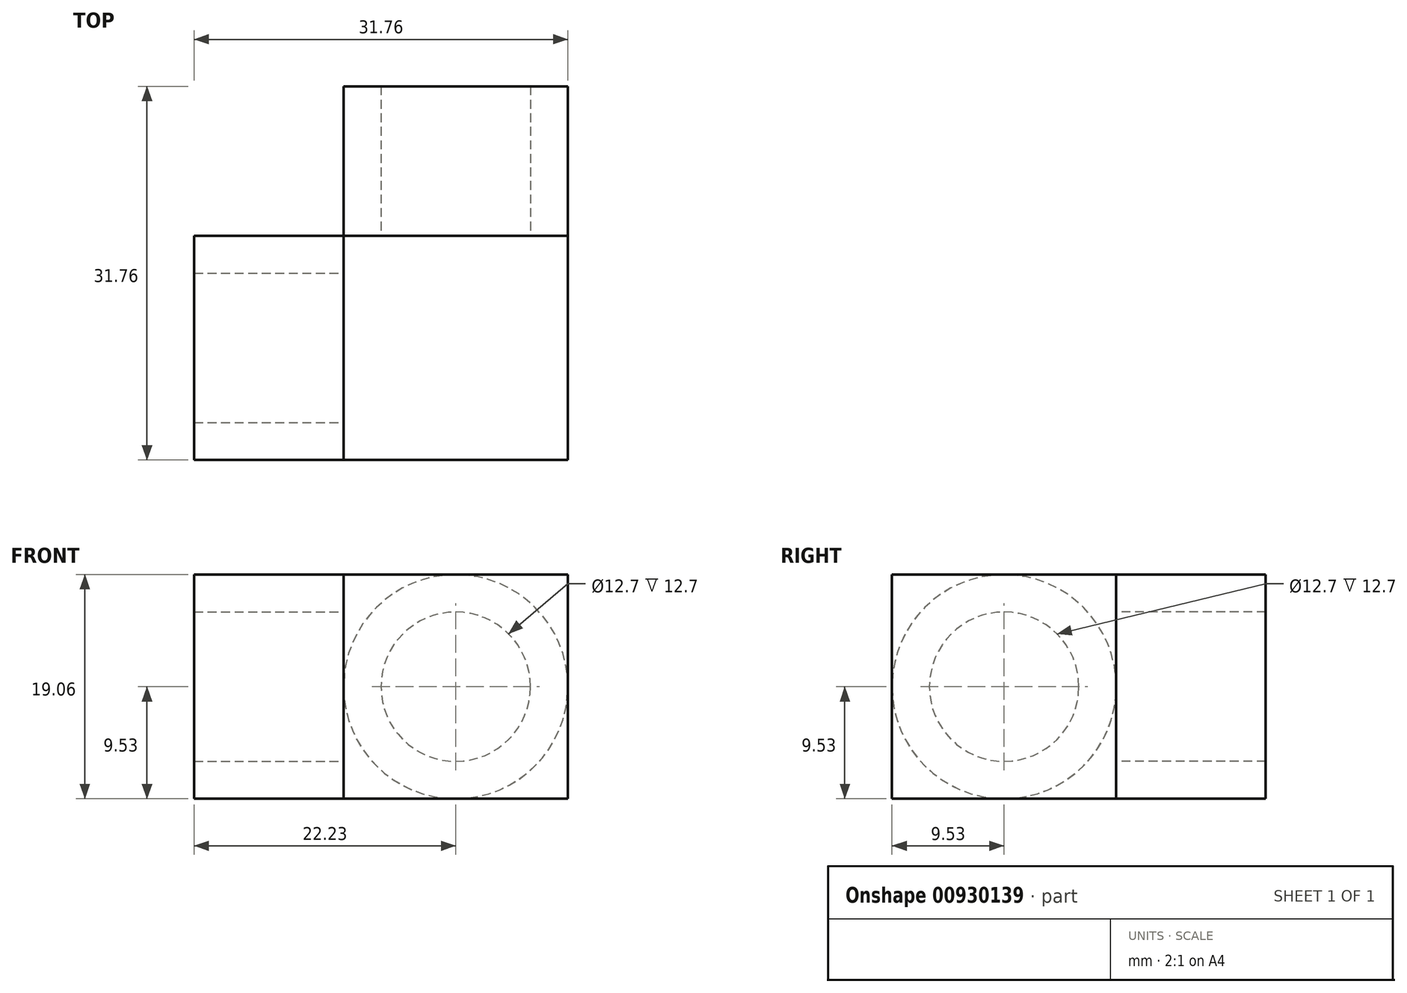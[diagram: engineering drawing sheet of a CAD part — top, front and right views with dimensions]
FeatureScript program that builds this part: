
annotation { "Feature Type Name" : "Feature", "Feature Type Description" : "" }
export const myFeature = defineFeature(function(context is Context, id is Id, definition is map)
    precondition{}
    {
        {
            var Q0;
            Q0=qCreatedBy(makeId("Top.planeOp"),FACE);
            var sketch = newSketch(context, id + "F0", { "sketchPlane" : qUnion([Q0])});
            skLineSegment(sketch, "E0.bottom", {"start": v(-9.53, -9.53) * mm, "end": v(9.53, -9.53) * mm});
            skLineSegment(sketch, "E0.top", {"start": v(-9.53, 9.53) * mm, "end": v(9.53, 9.53) * mm});
            skLineSegment(sketch, "E0.left", {"start": v(-9.53, -9.53) * mm, "end": v(-9.53, 9.53) * mm});
            skLineSegment(sketch, "E0.right", {"start": v(9.53, -9.52) * mm, "end": v(9.53, 9.53) * mm});
            skPoint(sketch, "E0.middle", {"position": v(0, 0) * mm});
            skSolve(sketch);
        }
        {
            var Q0;
            Q0 = qSketchRegion(id + "F0", true);
            extrude(context, id + "F1", {"entities" : qUnion([Q0]), "depth" : 19.05 * mm, "offsetDistance" : 25.4 * mm, "symmetric" : true});
        }
        {
            var Q0;
            Q0=makeQuery(id+"F1.opExtrude","SWEPT_FACE",FACE,{"disambiguationData":[OSD([sQuery(id+"F0.wireOp",EDGE,"E0.top")])]});
            var sketch = newSketch(context, id + "F2", { "sketchPlane" : qUnion([Q0])});
            skCircle(sketch, "E1", {"center": v(0, 0) * mm, "radius": 6.35 * mm});
            skCircle(sketch, "E2", {"center": v(0, 0) * mm, "radius": 9.53 * mm});
            skSolve(sketch);
        }
        {
            var Q0;
            Q0=makeQuery(id+"F2.imprint","IMPRINT",FACE,{"disambiguationData":[TD([[makeQuery(id+"F2.imprint","IMPRINT",EDGE,{"derivedFrom":sQuery(id+"F2.wireOp",EDGE,"E1")}),-1.0]])]});
            extrude(context, id + "F3", {"entities" : qUnion([Q0]), "operationType" : NewBodyOperationType.ADD, "depth" : 12.7 * mm, "offsetDistance" : 25.4 * mm});
        }
        {
            var Q0;
            Q0=makeQuery(id+"F1.opExtrude","SWEPT_FACE",FACE,{"disambiguationData":[OSD([sQuery(id+"F0.wireOp",EDGE,"E0.left")])]});
            var sketch = newSketch(context, id + "F4", { "sketchPlane" : qUnion([Q0])});
            skCircle(sketch, "E3", {"center": v(0, 0) * mm, "radius": 6.35 * mm});
            skCircle(sketch, "E4", {"center": v(0, 0) * mm, "radius": 9.53 * mm});
            skSolve(sketch);
        }
        {
            var Q0;
            Q0 = qSketchRegion(id + "F4", true);
            extrude(context, id + "F5", {"entities" : qUnion([Q0]), "operationType" : NewBodyOperationType.ADD, "depth" : 12.7 * mm, "offsetDistance" : 25.4 * mm});
        }
    });
